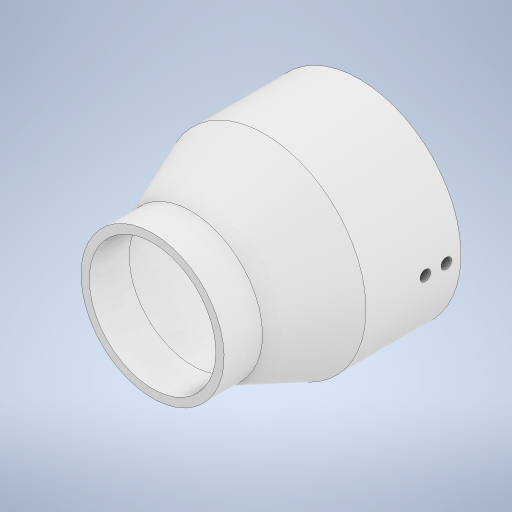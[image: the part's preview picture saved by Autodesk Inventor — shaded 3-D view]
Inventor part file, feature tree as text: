
AUTODESK INVENTOR PART (.ipt)
format: ipt  version: 2023 (Build 270158030, 158C)  size: 276,480 bytes
history: native  units: in
note: dims shown in document units (in); Inventor stores cm internally (conversion verified against a paired STEP export)
features: sketch x2, revolve x1, extrude x1
ambient origin geometry x8: Origin, YZ Plane, XZ Plane, XY Plane, X Axis, Y Axis, Z Axis, Center Point
bodies: Solid1 (feature_tree)
feature tree (4):
  revolve  "Revolution1"  [1 undecoded]
  extrude  "Extrusion1"  Depth=0.3937in
  sketch  "Sketch1"  dims[d0=2.375in d1=3.5in]
  sketch  "Sketch3"  dims[d2=0.75in d3=1.75in d4=0.154in d5=3.88in d6=2.0in d7=90.0deg d8=0.1969in d9=0.1969in d10=0.2756in d11=0.3937in d12=0.0in d13=0.0in]
note: 1 required parameter value undecoded (feature->parameter linkage not recoverable at this tier; creation-order binding heuristic only, values carry confidence <= 0.55)
